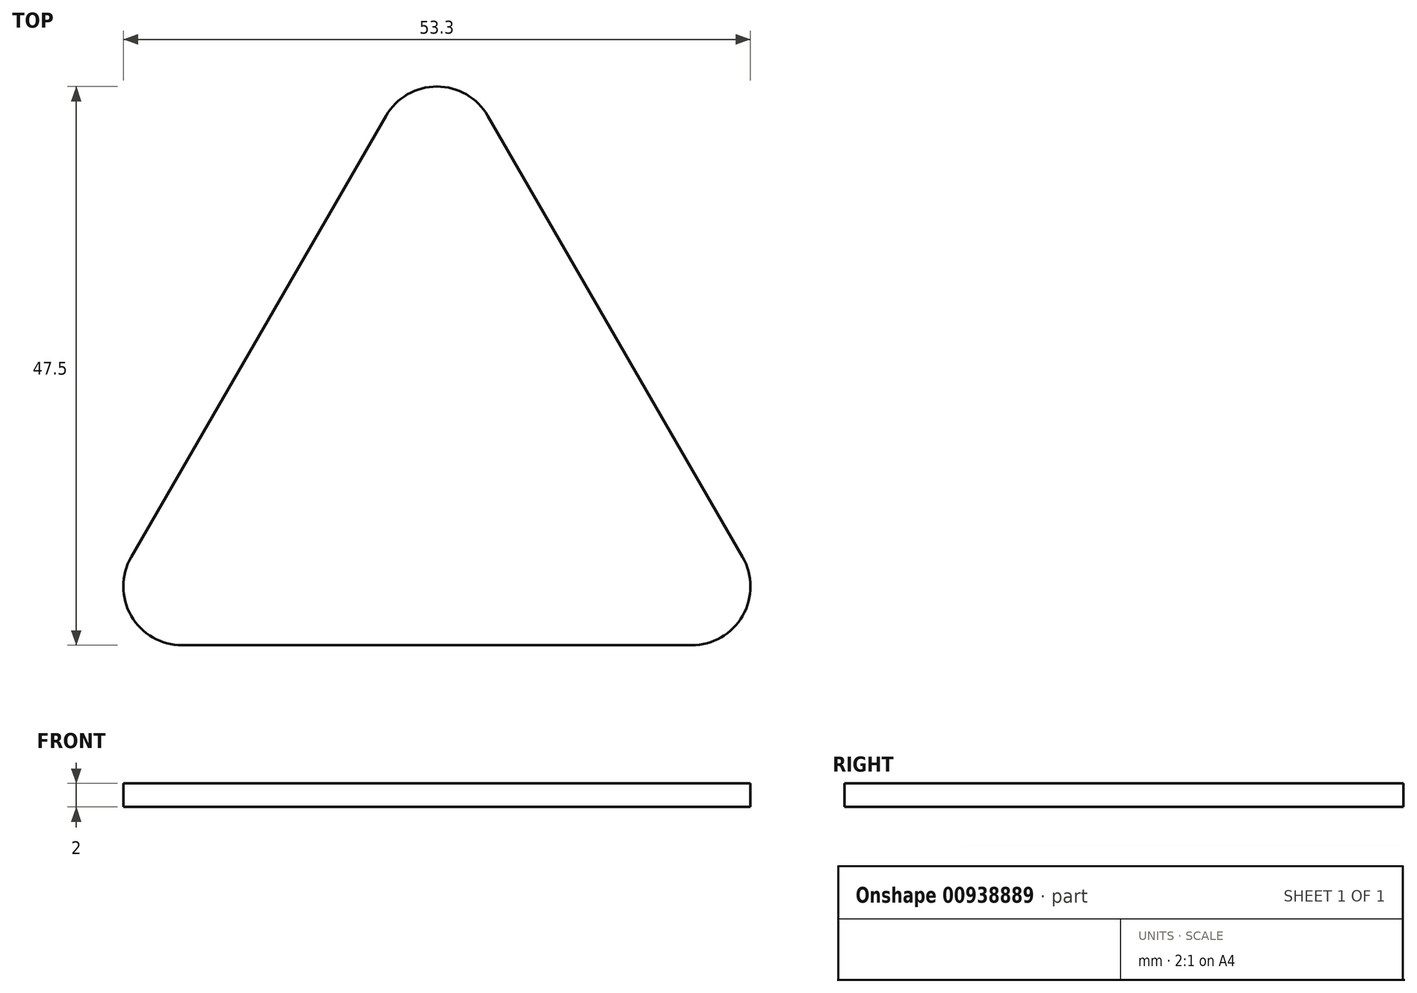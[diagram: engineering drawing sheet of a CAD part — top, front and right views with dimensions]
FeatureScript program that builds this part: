
annotation { "Feature Type Name" : "Feature", "Feature Type Description" : "" }
export const myFeature = defineFeature(function(context is Context, id is Id, definition is map)
    precondition{}
    {
        {
            var Q0;
            Q0=qCreatedBy(makeId("Top.planeOp"),FACE);
            var sketch = newSketch(context, id + "F0", { "sketchPlane" : qUnion([Q0])});
            skCircle(sketch, "E0.cCircle", {"center": v(0, 0) * mm, "radius": 35 * mm, "construction": true});
            skLineSegment(sketch, "E0.0", {"start": v(0, 35) * mm, "end": v(30.31, -17.5) * mm});
            skLineSegment(sketch, "E0.1", {"start": v(30.31, -17.5) * mm, "end": v(-30.31, -17.5) * mm});
            skLineSegment(sketch, "E0.2", {"start": v(-30.31, -17.5) * mm, "end": v(0, 35) * mm});
            skSolve(sketch);
        }
        {
            var Q0;
            Q0=makeQuery(id+"F0.imprint","IMPRINT",FACE,{"disambiguationData":[TD([[makeQuery(id+"F0.imprint","IMPRINT",EDGE,{"derivedFrom":sQuery(id+"F0.wireOp",EDGE,"E0.0")}),-1.0]])]});
            extrude(context, id + "F1", {"entities" : qUnion([Q0]), "depth" : 2 * mm, "offsetDistance" : 25 * mm});
        }
        {
            var Q0;
            Q0=makeQuery(id+"F1.opExtrude","SWEPT_EDGE",EDGE,{"disambiguationData":[OSD([sQuery(id+"F0.wireOp",EDGE,"E0.0"),sQuery(id+"F0.wireOp",EDGE,"E0.2")])]});
            var Q1;
            Q1=makeQuery(id+"F1.opExtrude","SWEPT_EDGE",EDGE,{"disambiguationData":[OSD([sQuery(id+"F0.wireOp",EDGE,"E0.1"),sQuery(id+"F0.wireOp",EDGE,"E0.2")])]});
            var Q2;
            Q2=makeQuery(id+"F1.opExtrude","SWEPT_EDGE",EDGE,{"disambiguationData":[OSD([sQuery(id+"F0.wireOp",EDGE,"E0.0"),sQuery(id+"F0.wireOp",EDGE,"E0.1")])]});
            fillet(context, id + "F2", {"entities" : qUnion([Q0, Q1, Q2]), "radius" : 5 * mm, "tangentPropagation" : true, "allowEdgeOverflow" : false});
        }
    });
